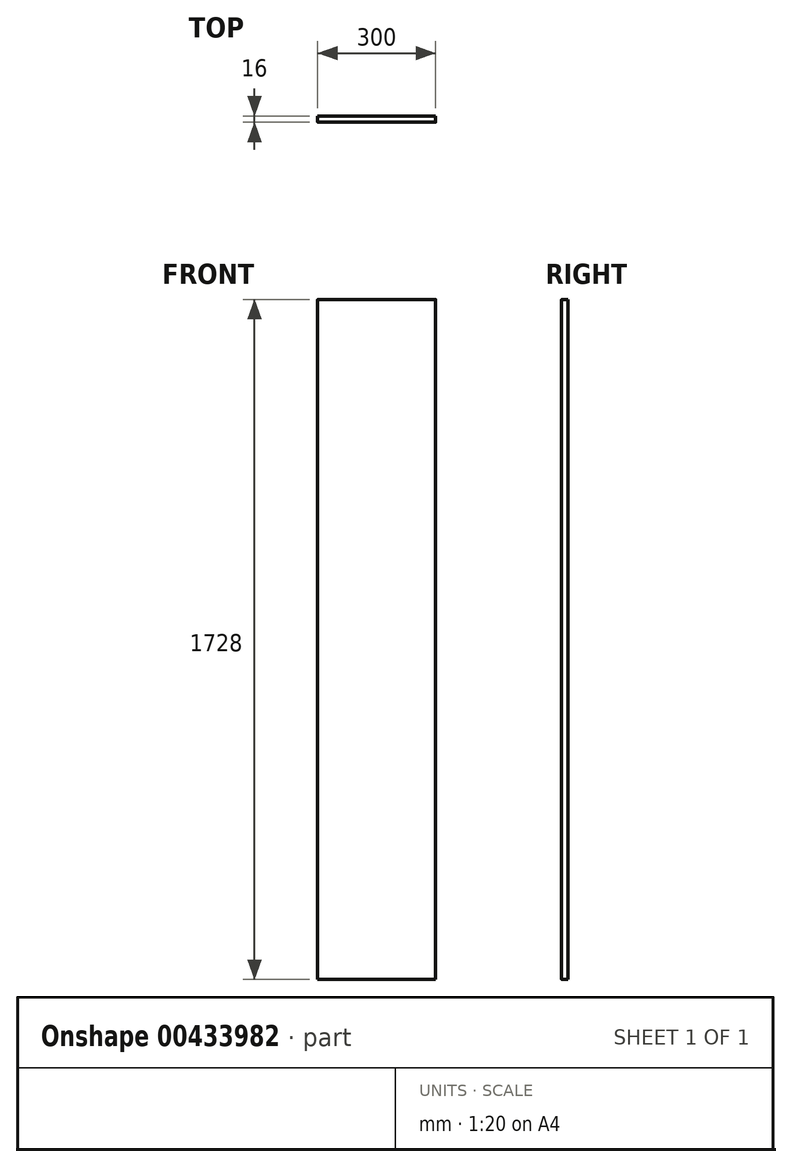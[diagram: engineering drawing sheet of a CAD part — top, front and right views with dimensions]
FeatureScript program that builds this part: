
annotation { "Feature Type Name" : "Feature", "Feature Type Description" : "" }
export const myFeature = defineFeature(function(context is Context, id is Id, definition is map)
    precondition{}
    {
        {
            var Q0;
            Q0=qCreatedBy(makeId("Front.planeOp"),FACE);
            var sketch = newSketch(context, id + "F0", { "sketchPlane" : qUnion([Q0])});
            skLineSegment(sketch, "E0.bottom", {"start": v(-145.56, 864) * mm, "end": v(154.44, 864) * mm});
            skLineSegment(sketch, "E0.top", {"start": v(-145.56, -864) * mm, "end": v(154.44, -864) * mm});
            skLineSegment(sketch, "E0.left", {"start": v(-145.56, 864) * mm, "end": v(-145.56, -864) * mm});
            skLineSegment(sketch, "E0.right", {"start": v(154.44, 864) * mm, "end": v(154.44, -864) * mm});
            skPoint(sketch, "E0.middle", {"position": v(4.44, 0) * mm});
            skSolve(sketch);
        }
        {
            var Q0;
            Q0 = qSketchRegion(id + "F0", true);
            extrude(context, id + "F1", {"entities" : qUnion([Q0]), "depth" : 16 * mm});
        }
        {
            var Q0;
            Q0=makeQuery(id+"F1.opExtrude","CAP_FACE",FACE,{"disambiguationData":[OSD([sQuery(id+"F0.wireOp",EDGE,"E0.bottom"),sQuery(id+"F0.wireOp",EDGE,"E0.top"),sQuery(id+"F0.wireOp",EDGE,"E0.left"),sQuery(id+"F0.wireOp",EDGE,"E0.right")])],"isStart":false});
            fillet(context, id + "F2", {"entities" : qUnion([Q0]), "radius" : 0.5 * mm, "tangentPropagation" : true, "allowEdgeOverflow" : false});
        }
        {
            var Q0;
            Q0=makeQuery(id+"F1.opExtrude","SWEPT_BODY",BODY,{"disambiguationData":[OSD([sQuery(id+"F0.wireOp",EDGE,"E0.bottom"),sQuery(id+"F0.wireOp",EDGE,"E0.top"),sQuery(id+"F0.wireOp",EDGE,"E0.left"),sQuery(id+"F0.wireOp",EDGE,"E0.right")])]});
            var Q1;
            Q1=makeQuery(id+"F1.opExtrude","CAP_EDGE",EDGE,{"disambiguationData":[OSD([sQuery(id+"F0.wireOp",EDGE,"E0.right")])],"isStart":true});
            transform(context, id + "F3", {"entities" : qUnion([Q0]), "transformType" : TransformType.ROTATION, "transformAxis" : qUnion([Q1]), "angle" : 180 * degree, "makeCopy" : true});
        }
        {
            var Q0;
            Q0=makeQuery(id+"F3.opPattern","COPY",BODY,{"derivedFrom":makeQuery(id+"F1.opExtrude","SWEPT_BODY",BODY,{"disambiguationData":[OSD([sQuery(id+"F0.wireOp",EDGE,"E0.bottom"),sQuery(id+"F0.wireOp",EDGE,"E0.top"),sQuery(id+"F0.wireOp",EDGE,"E0.left"),sQuery(id+"F0.wireOp",EDGE,"E0.right")])]}),"instanceName":"1"});
            var Q1;
            Q1=makeQuery(id+"F3.opPattern","COPY",FACE,{"derivedFrom":makeQuery(id+"F2.opFillet","BLEND_FACE",FACE,{"disambiguationData":[OSD([sQuery(id+"F0.wireOp",EDGE,"E0.bottom")])]}),"instanceName":"1"});
            var Q2;
            Q2=makeQuery(id+"F3.opPattern","COPY",FACE,{"derivedFrom":makeQuery(id+"F1.opExtrude","SWEPT_FACE",FACE,{"disambiguationData":[OSD([sQuery(id+"F0.wireOp",EDGE,"E0.bottom")])]}),"instanceName":"1"});
            transform(context, id + "F4", {"entities" : qUnion([Q0]), "transformType" : TransformType.TRANSLATION_DISTANCE, "transformDirection" : qUnion([Q1, Q2]), "distance" : 300 * mm, "makeCopy" : false});
        }
        {
            var Q0;
            Q0=makeQuery(id+"F3.opPattern","COPY",BODY,{"derivedFrom":makeQuery(id+"F1.opExtrude","SWEPT_BODY",BODY,{"disambiguationData":[OSD([sQuery(id+"F0.wireOp",EDGE,"E0.bottom"),sQuery(id+"F0.wireOp",EDGE,"E0.top"),sQuery(id+"F0.wireOp",EDGE,"E0.left"),sQuery(id+"F0.wireOp",EDGE,"E0.right")])]}),"instanceName":"1"});
            deleteBodies(context, id + "F5", {"entities" : qUnion([Q0])});
        }
    });
